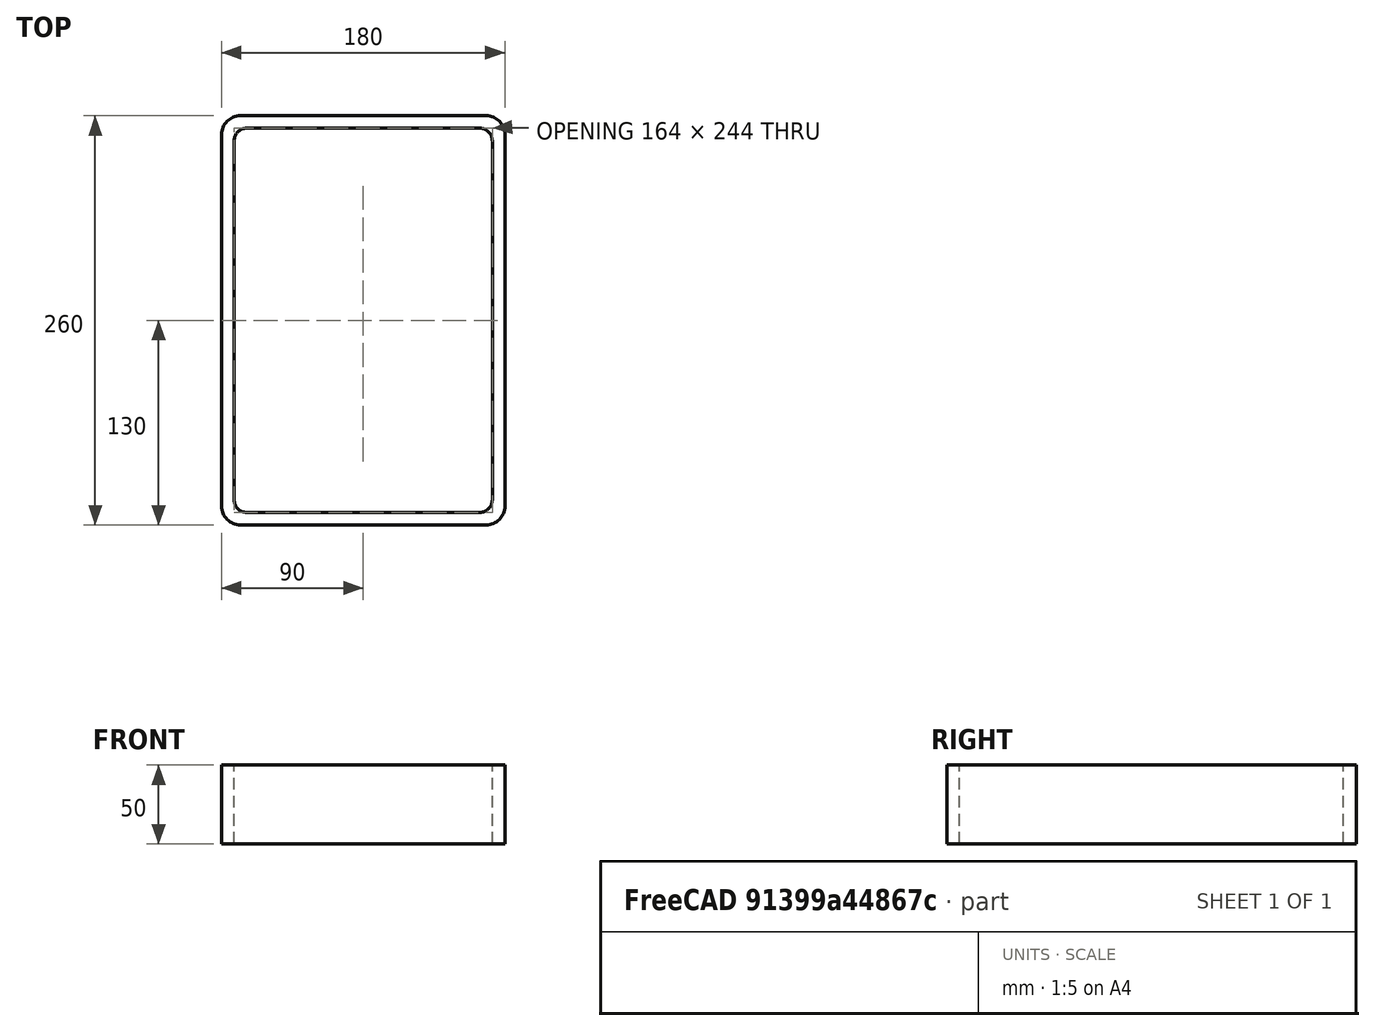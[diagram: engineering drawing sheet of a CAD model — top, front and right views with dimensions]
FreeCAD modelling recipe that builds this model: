
FCSTD DOCUMENT  (FreeCAD 0.15R4671 (Git))
Label: Rectangular hollow section 260x180x8 EN10219 S235JRH
License: All rights reserved
LicenseURL: http://en.wikipedia.org/wiki/All_rights_reserved
objects: Sketcher::SketchObject×1, Part::Extrusion×1
note: 2 computed .brp shape members not serialized (recipe doc carries the construction recipe); baked Part::Feature solids carry a one-line shape summary decoded from their .brp

FEATURE [Sketcher::SketchObject] Sketch
  sketch-geometry (16):
    g0: LineSegment StartX=-74 StartY=122 StartZ=0 EndX=74 EndY=122 EndZ=0
    g1: LineSegment StartX=82 StartY=114 StartZ=0 EndX=82 EndY=-114 EndZ=0
    g2: LineSegment StartX=74 StartY=-122 StartZ=0 EndX=-74 EndY=-122 EndZ=0
    g3: LineSegment StartX=-82 StartY=-114 StartZ=0 EndX=-82 EndY=114 EndZ=0
    g4: LineSegment StartX=-78 StartY=130 StartZ=0 EndX=78 EndY=130 EndZ=0
    g5: LineSegment StartX=90 StartY=118 StartZ=0 EndX=90 EndY=-118 EndZ=0
    g6: LineSegment StartX=78 StartY=-130 StartZ=0 EndX=-78 EndY=-130 EndZ=0
    g7: LineSegment StartX=-90 StartY=-118 StartZ=0 EndX=-90 EndY=118 EndZ=0
    g8: ArcOfCircle CenterX=-74 CenterY=114 CenterZ=0 NormalX=0 NormalY=0 NormalZ=1 Radius=8 StartAngle=1.5708 EndAngle=3.14159
    g9: ArcOfCircle CenterX=74 CenterY=114 CenterZ=0 NormalX=0 NormalY=0 NormalZ=1 Radius=8 StartAngle=0 EndAngle=1.5708
    g10: ArcOfCircle CenterX=74 CenterY=-114 CenterZ=0 NormalX=0 NormalY=0 NormalZ=1 Radius=8 StartAngle=4.71239 EndAngle=6.28319
    g11: ArcOfCircle CenterX=-74 CenterY=-114 CenterZ=0 NormalX=0 NormalY=0 NormalZ=1 Radius=8 StartAngle=3.14159 EndAngle=4.71239
    g12: ArcOfCircle CenterX=78 CenterY=118 CenterZ=0 NormalX=0 NormalY=0 NormalZ=1 Radius=12 StartAngle=0 EndAngle=1.5708
    g13: ArcOfCircle CenterX=78 CenterY=-118 CenterZ=0 NormalX=0 NormalY=0 NormalZ=1 Radius=12 StartAngle=4.71239 EndAngle=6.28319
    g14: ArcOfCircle CenterX=-78 CenterY=-118 CenterZ=0 NormalX=0 NormalY=0 NormalZ=1 Radius=12 StartAngle=3.14159 EndAngle=4.71239
    g15: ArcOfCircle CenterX=-78 CenterY=118 CenterZ=0 NormalX=0 NormalY=0 NormalZ=1 Radius=12 StartAngle=1.5708 EndAngle=3.14159
  constraints (36):
    c: Horizontal(g2)
    c: Vertical(g3)
    c: Horizontal(g6)
    c: Vertical(g7)
    c: Tangent(g3,g8) = 1.5708
    c: Tangent(g0,g8) = 1.5708
    c: Tangent(g0,g9) = 1.5708
    c: Tangent(g1,g9) = 1.5708
    c: Tangent(g1,g10) = 1.5708
    c: Tangent(g2,g10) = 1.5708
    c: Tangent(g2,g11) = 1.5708
    c: Tangent(g3,g11) = 1.5708
    c: Tangent(g4,g12) = 1.5708
    c: Tangent(g5,g12) = 1.5708
    c: Tangent(g5,g13) = 1.5708
    c: Tangent(g6,g13) = 1.5708
    c: Tangent(g6,g14) = 1.5708
    c: Tangent(g7,g14) = 1.5708
    c: Tangent(g7,g15) = 1.5708
    c: Tangent(g4,g15) = 1.5708
    c: Equal(g9,g8)
    c: Equal(g9,g11)
    c: Equal(g9,g10)
    c: Equal(g12,g15)
    c: Equal(g12,g14)
    c: Equal(g12,g13)
    c: Symmetric(g4,g6,g-1)
    c: Symmetric(g7,g5,g-2)
    c: DistanceY(g4,g6) = -260
    c: DistanceX(g7,g5) = 180
    c: Symmetric(g3,g1,g-2)
    c: Symmetric(g0,g2,g-1)
    c: DistanceY(g0,g4) = 8
    c: DistanceX(g5,g1) = -8
    c: Radius(g9) = 8
    c: Radius(g12) = 12
FEATURE [Part::Extrusion] Extrude  label="Rectangular hollow section 260x180x8 EN10219 S235JRH"
  Base = -> Sketch
  Dir = (0,0,50)
  Solid = true
